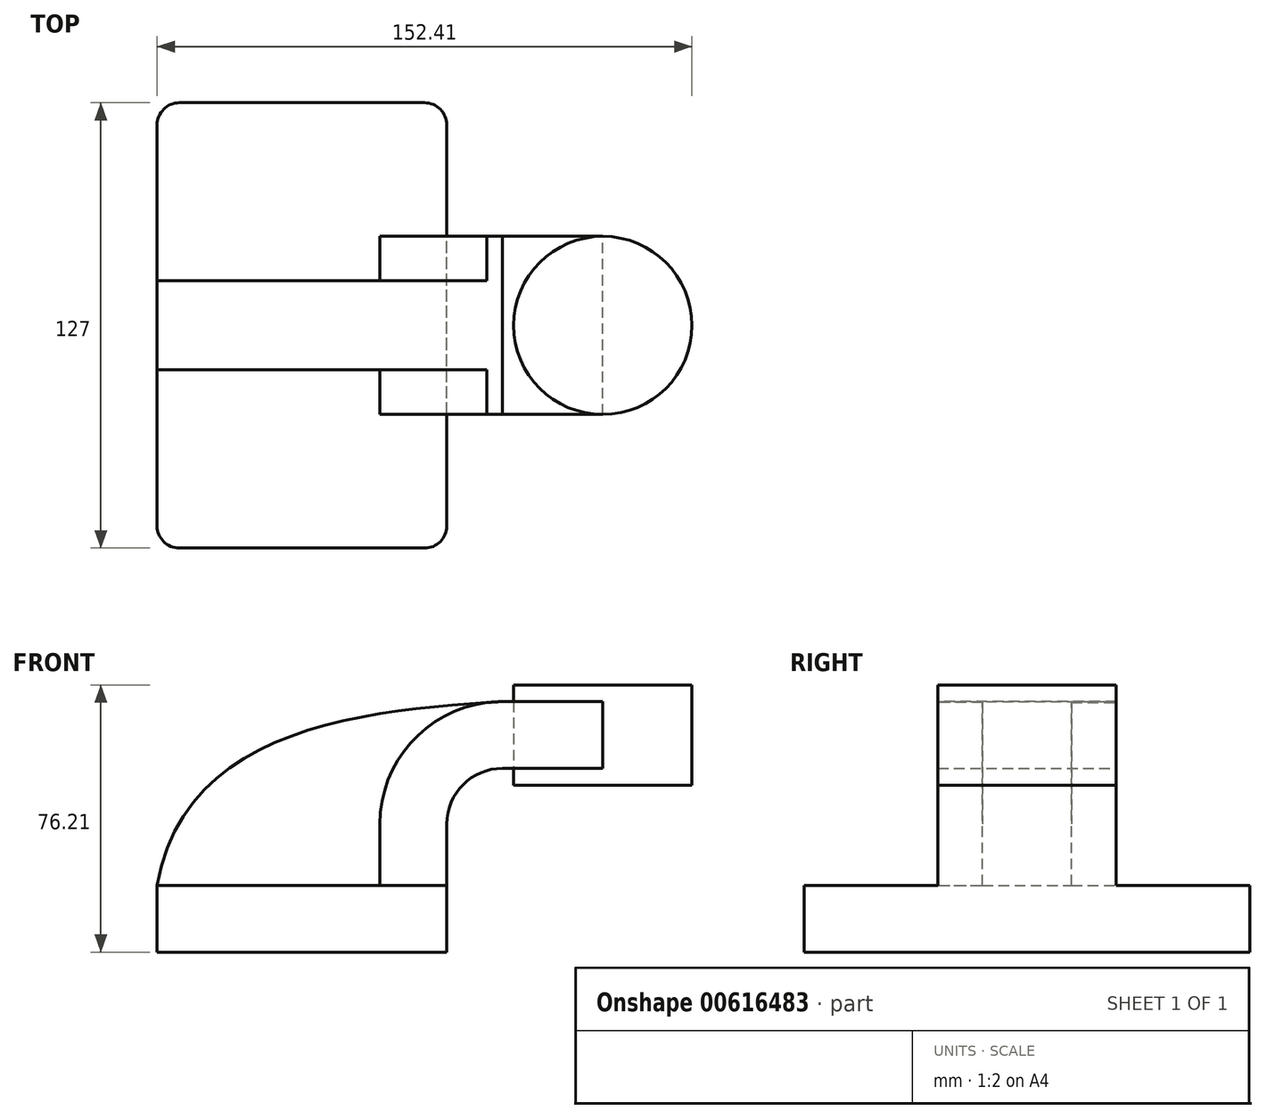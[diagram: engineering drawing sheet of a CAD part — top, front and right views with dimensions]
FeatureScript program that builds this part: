
annotation { "Feature Type Name" : "Feature", "Feature Type Description" : "" }
export const myFeature = defineFeature(function(context is Context, id is Id, definition is map)
    precondition{}
    {
        {
            var Q0;
            Q0=qCreatedBy(makeId("Front.planeOp"),FACE);
            var sketch = newSketch(context, id + "F0", { "sketchPlane" : qUnion([Q0])});
            skLineSegment(sketch, "E0.bottom", {"start": v(-41.28, -9.53) * mm, "end": v(41.28, -9.53) * mm});
            skLineSegment(sketch, "E0.top", {"start": v(-41.28, 9.53) * mm, "end": v(41.28, 9.53) * mm});
            skLineSegment(sketch, "E0.left", {"start": v(-41.28, -9.53) * mm, "end": v(-41.28, 9.53) * mm});
            skLineSegment(sketch, "E0.right", {"start": v(41.28, -9.53) * mm, "end": v(41.28, 9.53) * mm});
            skPoint(sketch, "E0.middle", {"position": v(0, 0) * mm});
            skLineSegment(sketch, "E1.bottom", {"start": v(60.33, 38.1) * mm, "end": v(111.12, 38.1) * mm});
            skLineSegment(sketch, "E1.top", {"start": v(60.33, 66.67) * mm, "end": v(111.12, 66.67) * mm});
            skLineSegment(sketch, "E1.left", {"start": v(60.33, 38.1) * mm, "end": v(60.33, 66.67) * mm});
            skLineSegment(sketch, "E1.right", {"start": v(111.12, 38.1) * mm, "end": v(111.12, 66.67) * mm});
            skPoint(sketch, "E1.middle", {"position": v(85.72, 52.39) * mm});
            skLineSegment(sketch, "E2", {"start": v(41.28, 9.53) * mm, "end": v(41.28, 27) * mm});
            skArc(sketch, "E3", {"start": v(41.27, 27) * mm, "mid": v(45.92, 38.23) * mm, "end": v(57.15, 42.88) * mm});
            skLineSegment(sketch, "E4", {"start": v(57.15, 42.88) * mm, "end": v(85.72, 42.88) * mm});
            skLineSegment(sketch, "E5.0", {"start": v(57.15, 61.93) * mm, "end": v(85.72, 61.93) * mm});
            skArc(sketch, "E5.1", {"start": v(22.22, 27) * mm, "mid": v(32.45, 51.7) * mm, "end": v(57.15, 61.93) * mm});
            skLineSegment(sketch, "E5.2", {"start": v(22.22, 9.53) * mm, "end": v(22.22, 27) * mm});
            skLineSegment(sketch, "E6", {"start": v(85.72, 38.1) * mm, "end": v(85.72, 66.67) * mm});
            skFitSpline(sketch, "E7", {"points": [v(-41.28, 9.52) * mm, v(57.15, 61.93) * mm], "startDerivative": vector(23.2, 137.27) * mm, "endDerivative": vector(112.32, 6.98) * mm});
            skSolve(sketch);
        }
        {
            var Q0;
            Q0=makeQuery(id+"F0.imprint","IMPRINT",FACE,{"disambiguationData":[TD([[makeQuery(id+"F0.imprint","IMPRINT",EDGE,{"derivedFrom":sQuery(id+"F0.wireOp",EDGE,"E0.bottom")}),1.0]])]});
            extrude(context, id + "F1", {"entities" : qUnion([Q0]), "endBound" : BoundingType.SYMMETRIC, "depth" : 127 * mm, "offsetDistance" : 25.4 * mm});
        }
        {
            var Q0;
            {var subQ1=sQuery(id+"F0.wireOp",EDGE,"E2");Q0=makeQuery(id+"F0.imprint","IMPRINT",FACE,{"disambiguationData":[TD([[makeQuery(id+"F0.imprint","IMPRINT",EDGE,{"derivedFrom":subQ1}),1.0]])]});}
            var Q1;
            {var subQ0=sQuery(id+"F0.wireOp",EDGE,"E4");var subQ1=sQuery(id+"F0.wireOp",EDGE,"E1.left");var subQ2=makeQuery(id+"F0.imprint","INTERSECT",VERTEX,{"derivedFrom":[subQ1,subQ0]});Q1=makeQuery(id+"F0.imprint","IMPRINT",FACE,{"disambiguationData":[TD([[makeQuery(id+"F0.imprint","IMPRINT",EDGE,{"disambiguationData":[TD([[subQ2,-1.0]])],"derivedFrom":subQ1}),-1.0]])]});}
            extrude(context, id + "F2", {"entities" : qUnion([Q0, Q1]), "operationType" : NewBodyOperationType.ADD, "endBound" : BoundingType.SYMMETRIC, "depth" : 50.8 * mm, "offsetDistance" : 25.4 * mm});
        }
        {
            var Q0;
            {var subQ3=sQuery(id+"F0.wireOp",EDGE,"E5.2");Q0=makeQuery(id+"F0.imprint","IMPRINT",FACE,{"disambiguationData":[TD([[makeQuery(id+"F0.imprint","IMPRINT",EDGE,{"derivedFrom":subQ3}),1.0]])]});}
            extrude(context, id + "F3", {"entities" : qUnion([Q0]), "operationType" : NewBodyOperationType.ADD, "endBound" : BoundingType.SYMMETRIC, "depth" : 25.4 * mm, "offsetDistance" : 25.4 * mm});
        }
        {
            var Q0;
            {var subQ4=sQuery(id+"F0.wireOp",EDGE,"E1.right");Q0=makeQuery(id+"F0.imprint","IMPRINT",FACE,{"disambiguationData":[TD([[makeQuery(id+"F0.imprint","IMPRINT",EDGE,{"derivedFrom":subQ4}),1.0]])]});}
            var Q1;
            Q1=sQuery(id+"F0.wireOp",EDGE,"E6");
            revolve(context, id + "F4", {"entities" : qUnion([Q0]), "axis" : qUnion([Q1]), "revolveType" : RevolveType.FULL});
        }
        {
            var Q0;
            Q0=makeQuery(id+"F1.opExtrude","CAP_EDGE",EDGE,{"disambiguationData":[OSD([sQuery(id+"F0.wireOp",EDGE,"E0.right")])],"isStart":false});
            var Q1;
            Q1=makeQuery(id+"F1.opExtrude","CAP_EDGE",EDGE,{"disambiguationData":[OSD([sQuery(id+"F0.wireOp",EDGE,"E0.left")])],"isStart":false});
            var Q2;
            Q2=makeQuery(id+"F1.opExtrude","CAP_EDGE",EDGE,{"disambiguationData":[OSD([sQuery(id+"F0.wireOp",EDGE,"E0.left")])],"isStart":true});
            var Q3;
            Q3=makeQuery(id+"F1.opExtrude","CAP_EDGE",EDGE,{"disambiguationData":[OSD([sQuery(id+"F0.wireOp",EDGE,"E0.right")])],"isStart":true});
            fillet(context, id + "F5", {"entities" : qUnion([Q0, Q1, Q2, Q3]), "radius" : 6.35 * mm, "tangentPropagation" : true, "allowEdgeOverflow" : false});
        }
    });
